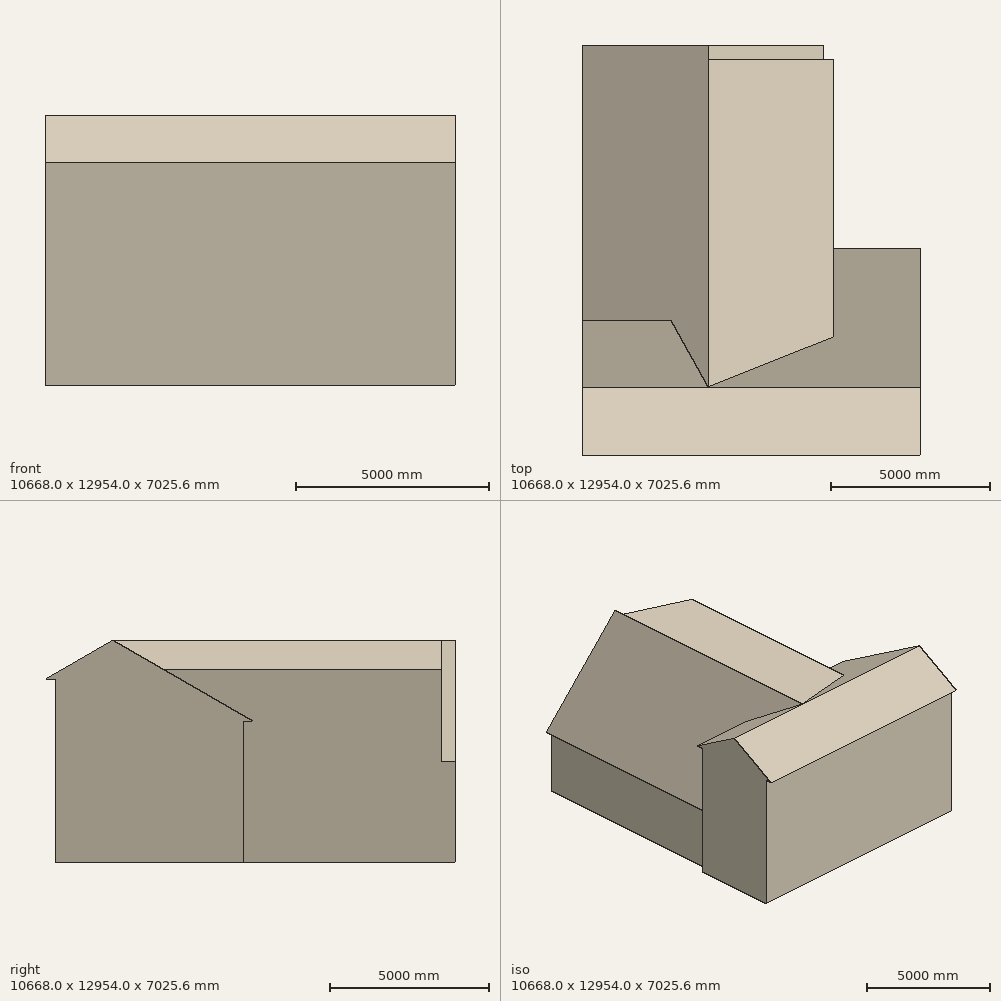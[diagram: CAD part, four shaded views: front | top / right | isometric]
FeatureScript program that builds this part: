
annotation { "Feature Type Name" : "Feature", "Feature Type Description" : "" }
export const myFeature = defineFeature(function(context is Context, id is Id, definition is map)
    precondition{}
    {
        {
            var Q0;
            Q0=qCreatedBy(makeId("Front.planeOp"),FACE);
            var sketch = newSketch(context, id + "F0", { "sketchPlane" : qUnion([Q0])});
            skLineSegment(sketch, "E0", {"start": v(0, 0) * mm, "end": v(0, 2895.6) * mm});
            skLineSegment(sketch, "E1", {"start": v(0, 2895.6) * mm, "end": v(-304.8, 2895.6) * mm});
            skLineSegment(sketch, "E2", {"start": v(-304.8, 2895.6) * mm, "end": v(3657.6, 7010.4) * mm});
            skLineSegment(sketch, "E3", {"start": v(7315.2, 6096) * mm, "end": v(7315.2, 0) * mm});
            skLineSegment(sketch, "E4", {"start": v(7315.2, 0) * mm, "end": v(0, 0) * mm});
            skLineSegment(sketch, "E5", {"start": v(3657.6, 0) * mm, "end": v(3657.6, 8986.38) * mm, "construction": true});
            skLineSegment(sketch, "E6", {"start": v(3657.6, 7010.4) * mm, "end": v(7620, 6096) * mm});
            skLineSegment(sketch, "E7", {"start": v(7620, 6096) * mm, "end": v(7315.2, 6096) * mm});
            skSolve(sketch);
        }
        {
            var Q0;
            Q0 = qSketchRegion(id + "F0", true);
            extrude(context, id + "F1", {"entities" : qUnion([Q0]), "depth" : 9753.6 * mm, "symmetric" : true});
        }
        {
            var Q0;
            Q0=makeQuery(id+"F1.opExtrude","CAP_FACE",FACE,{"disambiguationData":[OSD([sQuery(id+"F0.wireOp",EDGE,"E0"),sQuery(id+"F0.wireOp",EDGE,"E1"),sQuery(id+"F0.wireOp",EDGE,"E2"),sQuery(id+"F0.wireOp",EDGE,"E3"),sQuery(id+"F0.wireOp",EDGE,"E4"),sQuery(id+"F0.wireOp",EDGE,"E6"),sQuery(id+"F0.wireOp",EDGE,"E7")])],"isStart":true});
            var sketch = newSketch(context, id + "F2", { "sketchPlane" : qUnion([Q0])});
            skLineSegment(sketch, "E8", {"start": v(-3657.6, 7010.4) * mm, "end": v(-7620, 2895.6) * mm});
            skLineSegment(sketch, "E9", {"start": v(-3657.6, 7010.4) * mm, "end": v(-3657.6, 4471.94) * mm, "construction": true});
            skLineSegment(sketch, "E10", {"start": v(-3657.6, 7010.4) * mm, "end": v(-7620, 7010.4) * mm});
            skLineSegment(sketch, "E11", {"start": v(-7620, 7010.4) * mm, "end": v(-7620, 2895.6) * mm});
            skSolve(sketch);
        }
        {
            var Q0;
            Q0 = qSketchRegion(id + "F2", true);
            extrude(context, id + "F3", {"entities" : qUnion([Q0]), "operationType" : NewBodyOperationType.REMOVE, "oppositeDirection" : true, "depth" : 457.2 * mm});
        }
        {
            var Q0;
            Q0=makeQuery(id+"F1.opExtrude","SWEPT_FACE",FACE,{"disambiguationData":[OSD([sQuery(id+"F0.wireOp",EDGE,"E0")])]});
            var sketch = newSketch(context, id + "F4", { "sketchPlane" : qUnion([Q0])});
            skLineSegment(sketch, "E12.0", {"start": v(7772.4, 0) * mm, "end": v(4114.8, 0) * mm});
            skLineSegment(sketch, "E13", {"start": v(7772.4, 0) * mm, "end": v(7772.4, 5793.8) * mm});
            skLineSegment(sketch, "E14", {"start": v(7772.4, 5793.8) * mm, "end": v(8077.2, 5793.8) * mm});
            skLineSegment(sketch, "E15", {"start": v(8077.2, 5793.8) * mm, "end": v(5943.6, 7025.64) * mm});
            skLineSegment(sketch, "E16", {"start": v(5943.6, 7025.64) * mm, "end": v(3810, 5793.8) * mm});
            skLineSegment(sketch, "E17", {"start": v(3810, 5793.8) * mm, "end": v(4114.8, 5793.8) * mm});
            skLineSegment(sketch, "E18", {"start": v(4114.8, 5793.8) * mm, "end": v(4114.8, 0) * mm});
            skPoint(sketch, "E19.orphan", {"position": v(4876.8, 0) * mm});
            skPoint(sketch, "E20.orphan", {"position": v(-4876.8, 0) * mm});
            skLineSegment(sketch, "E21", {"start": v(5943.6, 7025.64) * mm, "end": v(5943.6, 3373.28) * mm, "construction": true});
            skSolve(sketch);
        }
        {
            var Q0;
            Q0 = qSketchRegion(id + "F4", true);
            extrude(context, id + "F5", {"entities" : qUnion([Q0]), "operationType" : NewBodyOperationType.ADD, "oppositeDirection" : true, "depth" : 10363.2 * mm, "hasSecondDirection" : true, "secondDirectionOppositeDirection" : false, "secondDirectionDepth" : 304.8 * mm});
        }
        {
            var Q0;
            Q0=makeQuery(id+"F1.opExtrude","CAP_FACE",FACE,{"disambiguationData":[OSD([sQuery(id+"F0.wireOp",EDGE,"E0"),sQuery(id+"F0.wireOp",EDGE,"E1"),sQuery(id+"F0.wireOp",EDGE,"E2"),sQuery(id+"F0.wireOp",EDGE,"E3"),sQuery(id+"F0.wireOp",EDGE,"E4"),sQuery(id+"F0.wireOp",EDGE,"E6"),sQuery(id+"F0.wireOp",EDGE,"E7")])],"isStart":false});
            var sketch = newSketch(context, id + "F6", { "sketchPlane" : qUnion([Q0])});
            skLineSegment(sketch, "E22.0.0", {"start": v(3079.17, 6409.72) * mm, "end": v(6260.53, 6409.72) * mm});
            skLineSegment(sketch, "E22.0.1", {"start": v(6260.53, 6409.72) * mm, "end": v(3657.6, 7010.4) * mm});
            skLineSegment(sketch, "E22.0.2", {"start": v(3657.6, 7010.4) * mm, "end": v(3079.17, 6409.72) * mm});
            skSolve(sketch);
        }
        {
            var Q0;
            Q0 = qSketchRegion(id + "F6", true);
            var Q1;
            Q1=makeQuery(id+"F5.opExtrude","SWEPT_FACE",FACE,{"disambiguationData":[OSD([sQuery(id+"F4.wireOp",EDGE,"E16")])]});
            extrude(context, id + "F7", {"entities" : qUnion([Q0]), "operationType" : NewBodyOperationType.ADD, "endBound" : BoundingType.UP_TO_SURFACE, "endBoundEntityFace" : qUnion([Q1]), "depth" : 30.48 * mm});
        }
        {
            var Q0;
            Q0=makeQuery(id+"F5.opExtrude","CAP_FACE",FACE,{"disambiguationData":[OSD([sQuery(id+"F4.wireOp",EDGE,"E12.0"),sQuery(id+"F4.wireOp",EDGE,"E13"),sQuery(id+"F4.wireOp",EDGE,"E14"),sQuery(id+"F4.wireOp",EDGE,"E15"),sQuery(id+"F4.wireOp",EDGE,"E16"),sQuery(id+"F4.wireOp",EDGE,"E17"),sQuery(id+"F4.wireOp",EDGE,"E18")])],"isStart":false});
            var sketch = newSketch(context, id + "F8", { "sketchPlane" : qUnion([Q0])});
            skLineSegment(sketch, "E23.0", {"start": v(-4114.8, 0) * mm, "end": v(-1828.8, 0) * mm});
            skLineSegment(sketch, "E24.0", {"start": v(-4114.8, 5793.8) * mm, "end": v(-4114.8, 0) * mm});
            skLineSegment(sketch, "E25", {"start": v(-1828.8, 0) * mm, "end": v(-1828.8, 4473.98) * mm});
            skLineSegment(sketch, "E26", {"start": v(-1524, 4473.98) * mm, "end": v(-3810, 5793.8) * mm});
            skPoint(sketch, "E27.orphan", {"position": v(4876.8, 0) * mm});
            skLineSegment(sketch, "E28", {"start": v(-1828.8, 4473.98) * mm, "end": v(-1524, 4473.98) * mm});
            skLineSegment(sketch, "E29.0", {"start": v(-3810, 5793.8) * mm, "end": v(-4114.8, 5793.8) * mm});
            skSolve(sketch);
        }
        {
            var Q0;
            Q0 = qSketchRegion(id + "F8", true);
            var Q1;
            Q1=makeQuery(id+"F1.opExtrude","SWEPT_FACE",FACE,{"disambiguationData":[OSD([sQuery(id+"F0.wireOp",EDGE,"E3")])]});
            extrude(context, id + "F9", {"entities" : qUnion([Q0]), "operationType" : NewBodyOperationType.ADD, "endBound" : BoundingType.UP_TO_NEXT, "oppositeDirection" : true, "endBoundEntity" : qUnion([Q1]), "depth" : 30.48 * mm});
        }
    });
